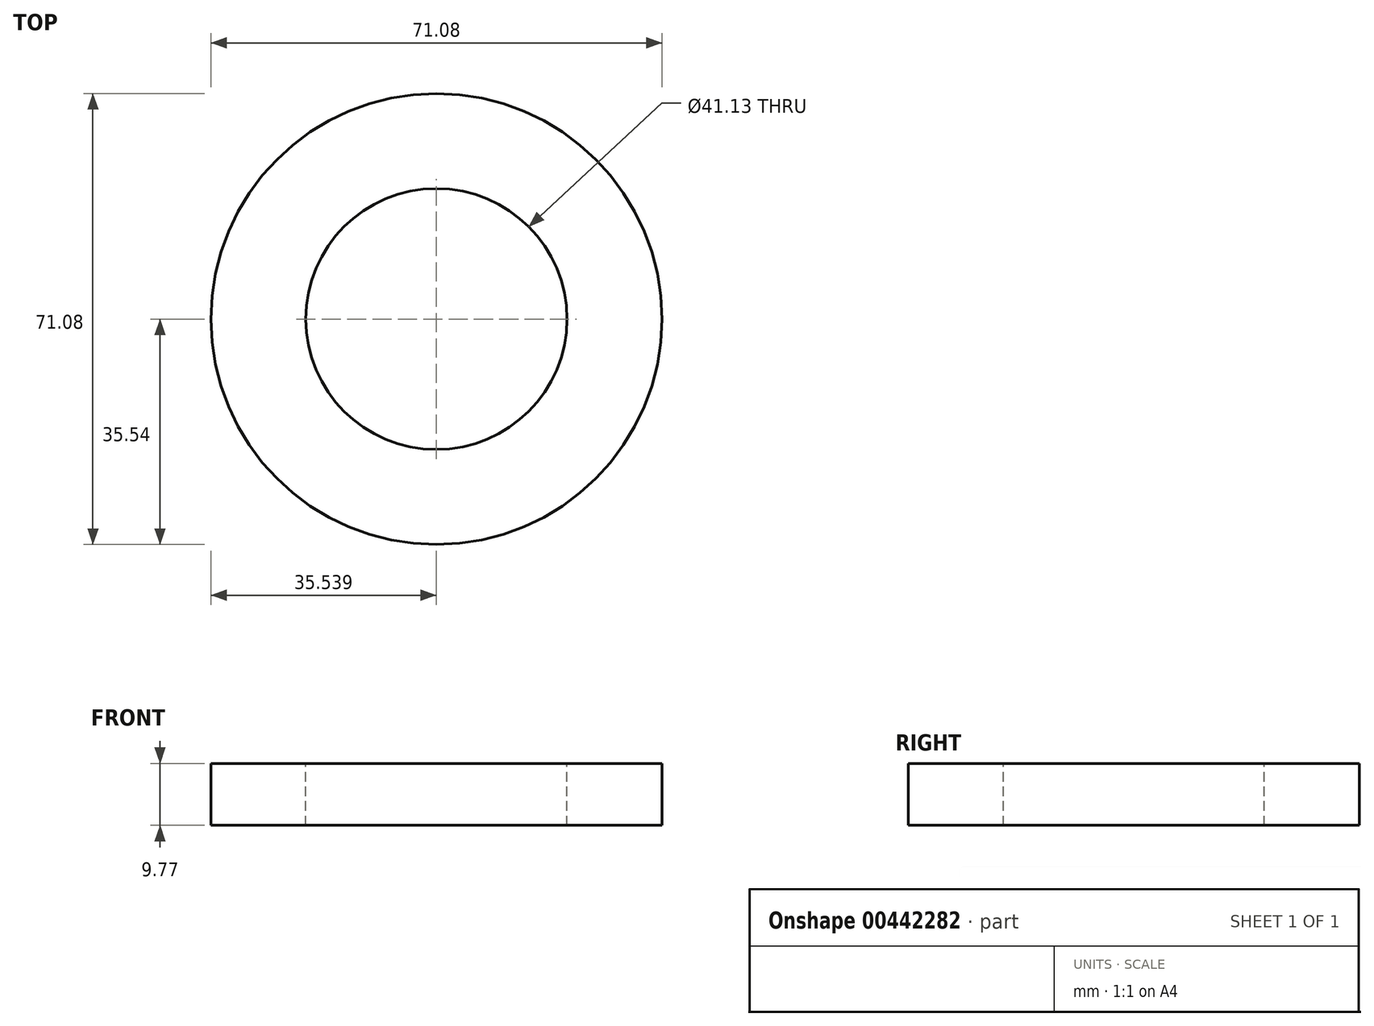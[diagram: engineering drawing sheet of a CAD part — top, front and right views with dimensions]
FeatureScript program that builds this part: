
annotation { "Feature Type Name" : "Feature", "Feature Type Description" : "" }
export const myFeature = defineFeature(function(context is Context, id is Id, definition is map)
    precondition{}
    {
        {
            var Q0;
            Q0=qCreatedBy(makeId("Front.planeOp"),FACE);
            var sketch = newSketch(context, id + "F0", { "sketchPlane" : qUnion([Q0])});
            skLineSegment(sketch, "E0.bottom", {"start": v(-22.91, 11.1) * mm, "end": v(-7.94, 11.1) * mm});
            skLineSegment(sketch, "E0.top", {"start": v(-22.91, 1.53) * mm, "end": v(-7.94, 1.53) * mm});
            skLineSegment(sketch, "E0.left", {"start": v(-22.91, 11.1) * mm, "end": v(-22.91, 1.53) * mm});
            skLineSegment(sketch, "E0.right", {"start": v(-7.94, 11.1) * mm, "end": v(-7.94, 6.31) * mm});
            skPoint(sketch, "E1.firstSnap0", {"position": v(-7.94, 6.31) * mm});
            skLineSegment(sketch, "E1.bottom", {"start": v(-7.94, 6.31) * mm, "end": v(12.63, 6.31) * mm});
            skLineSegment(sketch, "E1.top", {"start": v(-7.94, 1.53) * mm, "end": v(12.63, 1.53) * mm});
            skLineSegment(sketch, "E1.right", {"start": v(12.63, 6.31) * mm, "end": v(12.63, 1.53) * mm});
            skSolve(sketch);
        }
        {
            var Q0;
            Q0=makeQuery(id+"F0.imprint","IMPRINT",FACE,{"disambiguationData":[TD([[makeQuery(id+"F0.imprint","IMPRINT",EDGE,{"derivedFrom":sQuery(id+"F0.wireOp",EDGE,"E0.bottom")}),-1.0]])]});
            var Q1;
            Q1=sQuery(id+"F0.wireOp",EDGE,"E1.right");
            revolve(context, id + "F1", {"entities" : qUnion([Q0]), "axis" : qUnion([Q1]), "revolveType" : RevolveType.FULL});
        }
        {
            var Q0;
            Q0=makeQuery(id+"F1.opRevolve","SWEPT_FACE",FACE,{"disambiguationData":[OSD([sQuery(id+"F0.wireOp",EDGE,"E1.bottom")])]});
            extrude(context, id + "F2", {"entities" : qUnion([Q0]), "operationType" : NewBodyOperationType.REMOVE, "oppositeDirection" : true, "depth" : 25 * mm});
        }
        {
            var Q0;
            Q0=makeQuery(id+"F1.opRevolve","SWEPT_FACE",FACE,{"disambiguationData":[OSD([sQuery(id+"F0.wireOp",EDGE,"E0.top"),sQuery(id+"F0.wireOp",EDGE,"E1.top")])]});
            var Q1;
            Q1=makeQuery(id+"F1.opRevolve","SWEPT_FACE",FACE,{"disambiguationData":[OSD([sQuery(id+"F0.wireOp",EDGE,"E0.bottom")])]});
            extrude(context, id + "F3", {"entities" : qUnion([Q0, Q1]), "operationType" : NewBodyOperationType.ADD, "oppositeDirection" : true, "depth" : 0.2 * mm});
        }
    });
